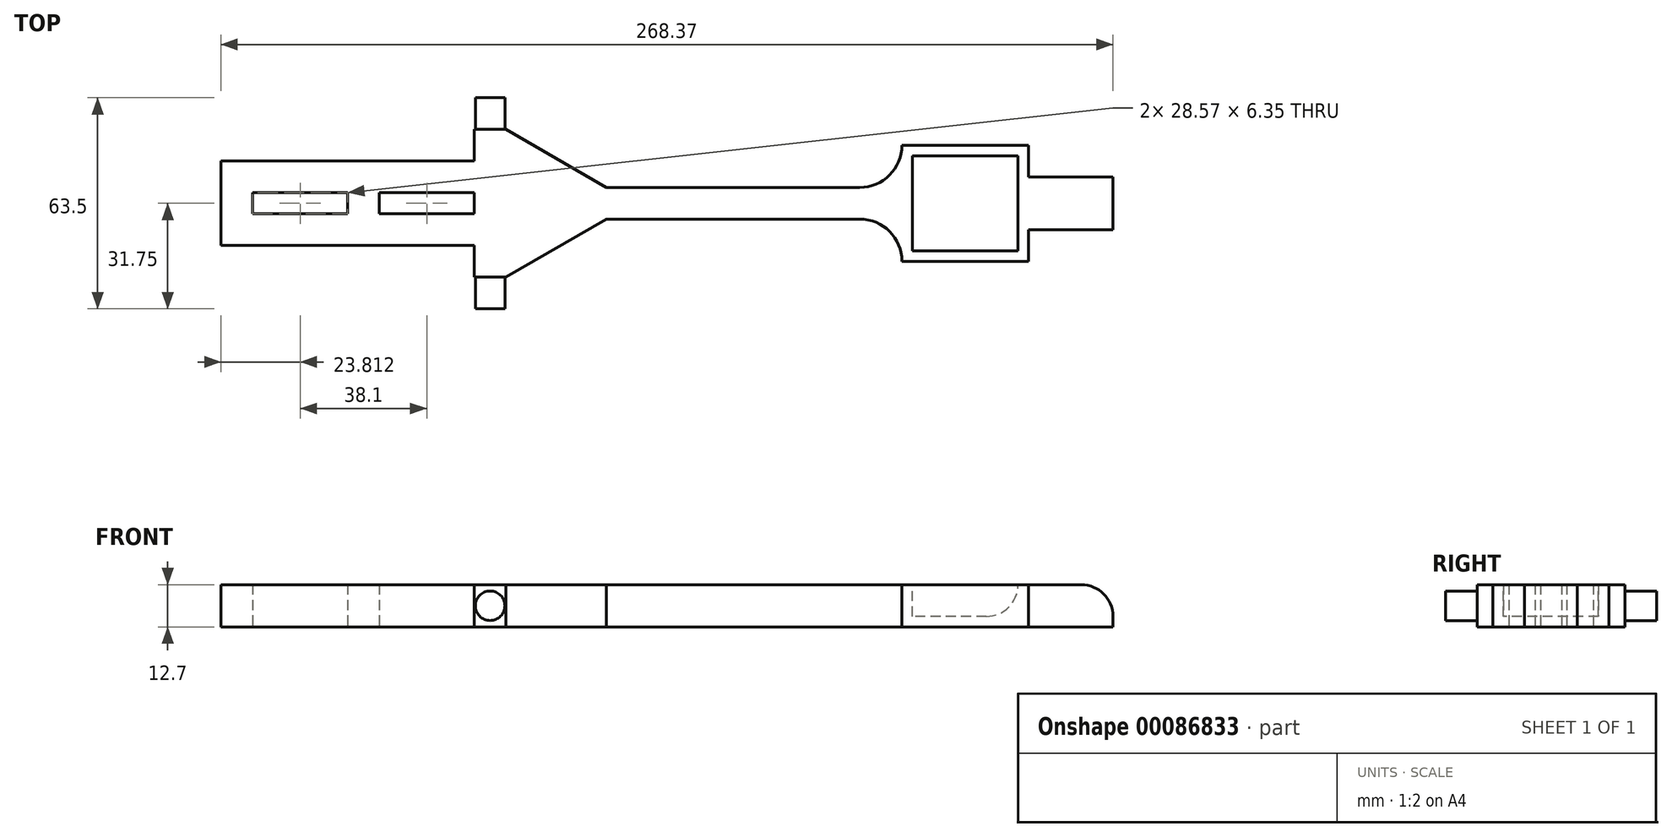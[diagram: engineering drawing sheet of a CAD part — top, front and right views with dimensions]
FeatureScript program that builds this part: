
annotation { "Feature Type Name" : "Feature", "Feature Type Description" : "" }
export const myFeature = defineFeature(function(context is Context, id is Id, definition is map)
    precondition{}
    {
        {
            var Q0;
            Q0=qCreatedBy(makeId("Top.planeOp"),FACE);
            var sketch = newSketch(context, id + "F0", { "sketchPlane" : qUnion([Q0])});
            skLineSegment(sketch, "E0.bottom", {"start": v(0, -12.7) * mm, "end": v(-76.2, -12.7) * mm});
            skLineSegment(sketch, "E0.top", {"start": v(0, 12.7) * mm, "end": v(-76.2, 12.7) * mm});
            skLineSegment(sketch, "E0.left", {"start": v(0, -3.17) * mm, "end": v(0, 3.17) * mm});
            skLineSegment(sketch, "E0.right", {"start": v(-76.2, -12.7) * mm, "end": v(-76.2, 12.7) * mm});
            skLineSegment(sketch, "E1.bottom", {"start": v(0, -3.17) * mm, "end": v(-28.58, -3.17) * mm});
            skLineSegment(sketch, "E1.top", {"start": v(0, 3.17) * mm, "end": v(-28.58, 3.17) * mm});
            skLineSegment(sketch, "E1.right", {"start": v(-28.58, -3.17) * mm, "end": v(-28.58, 3.17) * mm});
            skLineSegment(sketch, "E2.bottom", {"start": v(-66.68, 3.17) * mm, "end": v(-38.1, 3.17) * mm});
            skLineSegment(sketch, "E2.top", {"start": v(-66.68, -3.17) * mm, "end": v(-38.1, -3.17) * mm});
            skLineSegment(sketch, "E2.left", {"start": v(-66.68, 3.18) * mm, "end": v(-66.68, -3.18) * mm});
            skLineSegment(sketch, "E2.right", {"start": v(-38.1, 3.18) * mm, "end": v(-38.1, -3.18) * mm});
            skLineSegment(sketch, "E3", {"start": v(-76.2, 0) * mm, "end": v(-66.68, 0) * mm, "construction": true});
            skLineSegment(sketch, "E4", {"start": v(-52.39, 12.7) * mm, "end": v(-52.39, 3.18) * mm, "construction": true});
            skLineSegment(sketch, "E5", {"start": v(-38.1, 0) * mm, "end": v(-28.58, 0) * mm, "construction": true});
            skPoint(sketch, "E5.startSnap0", {"position": v(-38.1, 0) * mm});
            skLineSegment(sketch, "E6", {"start": v(-14.29, 3.17) * mm, "end": v(-14.29, 12.7) * mm, "construction": true});
            skLineSegment(sketch, "E7.bottom", {"start": v(0, 22.23) * mm, "end": v(9.53, 22.23) * mm});
            skLineSegment(sketch, "E7.top", {"start": v(0, -22.23) * mm, "end": v(9.53, -22.23) * mm});
            skLineSegment(sketch, "E7.left", {"start": v(0, 22.23) * mm, "end": v(0, 12.7) * mm});
            skLineSegment(sketch, "E7.right", {"start": v(9.53, 22.22) * mm, "end": v(9.53, -22.22) * mm, "construction": true});
            skLineSegment(sketch, "E8", {"start": v(-52.39, -3.18) * mm, "end": v(-52.39, -12.7) * mm, "construction": true});
            skLineSegment(sketch, "E9.trimOffspring", {"start": v(0, 3.18) * mm, "end": v(0, -3.17) * mm});
            skLineSegment(sketch, "E10.trimOffspring", {"start": v(0, -12.7) * mm, "end": v(0, -22.23) * mm});
            skPoint(sketch, "E11.endSnap0", {"position": v(9.52, 0) * mm});
            skLineSegment(sketch, "E12", {"start": v(9.52, 22.23) * mm, "end": v(39.77, 4.76) * mm});
            skLineSegment(sketch, "E13", {"start": v(39.77, -4.76) * mm, "end": v(9.52, -22.23) * mm});
            skLineSegment(sketch, "E14.bottom", {"start": v(39.77, 4.76) * mm, "end": v(115.97, 4.76) * mm});
            skLineSegment(sketch, "E14.top", {"start": v(39.77, -4.76) * mm, "end": v(115.97, -4.76) * mm});
            skLineSegment(sketch, "E14.left", {"start": v(39.77, 4.76) * mm, "end": v(39.77, -4.76) * mm, "construction": true});
            skArc(sketch, "E15", {"start": v(115.97, 4.76) * mm, "mid": v(124.95, 8.48) * mm, "end": v(128.67, 17.46) * mm});
            skArc(sketch, "E16", {"start": v(128.67, -17.46) * mm, "mid": v(124.95, -8.48) * mm, "end": v(115.97, -4.76) * mm});
            skLineSegment(sketch, "E17.bottom", {"start": v(128.67, 17.46) * mm, "end": v(166.77, 17.46) * mm});
            skLineSegment(sketch, "E17.top", {"start": v(128.67, -17.46) * mm, "end": v(166.77, -17.46) * mm});
            skLineSegment(sketch, "E17.right", {"start": v(166.77, 17.46) * mm, "end": v(166.77, 7.94) * mm});
            skLineSegment(sketch, "E18.bottom", {"start": v(166.77, 7.94) * mm, "end": v(192.17, 7.94) * mm});
            skLineSegment(sketch, "E18.top", {"start": v(166.77, -7.94) * mm, "end": v(192.17, -7.94) * mm});
            skLineSegment(sketch, "E18.right", {"start": v(192.17, 7.94) * mm, "end": v(192.17, -7.94) * mm});
            skLineSegment(sketch, "E19.trimOffspring", {"start": v(166.77, -7.94) * mm, "end": v(166.77, -17.46) * mm});
            skLineSegment(sketch, "E20", {"start": v(9.52, 0) * mm, "end": v(39.77, 0) * mm, "construction": true});
            skSolve(sketch);
        }
        {
            var Q0;
            Q0=makeQuery(id+"F0.imprint","IMPRINT",FACE,{"disambiguationData":[TD([[makeQuery(id+"F0.imprint","IMPRINT",EDGE,{"derivedFrom":sQuery(id+"F0.wireOp",EDGE,"E0.bottom")}),-1.0]])]});
            extrude(context, id + "F1", {"entities" : qUnion([Q0]), "depth" : 12.7 * mm});
        }
        {
            var Q0;
            Q0=makeQuery(id+"F1.opExtrude","SWEPT_FACE",FACE,{"disambiguationData":[OSD([sQuery(id+"F0.wireOp",EDGE,"E7.top")])]});
            var sketch = newSketch(context, id + "F2", { "sketchPlane" : qUnion([Q0])});
            skCircle(sketch, "E21", {"center": v(4.76, 6.35) * mm, "radius": 4.45 * mm});
            skPoint(sketch, "E21.centerSnap0", {"position": v(4.76, 12.7) * mm});
            skLineSegment(sketch, "E22", {"start": v(0, 12.7) * mm, "end": v(9.52, 0) * mm, "construction": true});
            skSolve(sketch);
        }
        {
            var Q0;
            Q0=makeQuery(id+"F2.imprint","IMPRINT",FACE,{"disambiguationData":[TD([[makeQuery(id+"F2.imprint","IMPRINT",EDGE,{"derivedFrom":sQuery(id+"F2.wireOp",EDGE,"E21")}),1.0]])]});
            extrude(context, id + "F3", {"entities" : qUnion([Q0]), "operationType" : NewBodyOperationType.ADD, "depth" : 9.52 * mm});
        }
        {
            var Q0;
            Q0=makeQuery(id+"F1.opExtrude","SWEPT_FACE",FACE,{"disambiguationData":[OSD([sQuery(id+"F0.wireOp",EDGE,"E7.bottom")])]});
            var sketch = newSketch(context, id + "F4", { "sketchPlane" : qUnion([Q0])});
            skCircle(sketch, "E23.0", {"center": v(-4.76, 6.35) * mm, "radius": 4.45 * mm});
            skSolve(sketch);
        }
        {
            var Q0;
            Q0 = qSketchRegion(id + "F4", true);
            extrude(context, id + "F5", {"entities" : qUnion([Q0]), "operationType" : NewBodyOperationType.ADD, "depth" : 9.52 * mm});
        }
        {
            var Q0;
            Q0=makeQuery(id+"F1.opExtrude","CAP_FACE",FACE,{"disambiguationData":[OSD([sQuery(id+"F0.wireOp",EDGE,"E0.bottom"),sQuery(id+"F0.wireOp",EDGE,"E0.top"),sQuery(id+"F0.wireOp",EDGE,"E0.right"),sQuery(id+"F0.wireOp",EDGE,"E1.bottom"),sQuery(id+"F0.wireOp",EDGE,"E1.top"),sQuery(id+"F0.wireOp",EDGE,"E1.right"),sQuery(id+"F0.wireOp",EDGE,"E2.bottom"),sQuery(id+"F0.wireOp",EDGE,"E2.top"),sQuery(id+"F0.wireOp",EDGE,"E2.left"),sQuery(id+"F0.wireOp",EDGE,"E2.right"),sQuery(id+"F0.wireOp",EDGE,"E7.bottom"),sQuery(id+"F0.wireOp",EDGE,"E7.top"),sQuery(id+"F0.wireOp",EDGE,"E7.left"),sQuery(id+"F0.wireOp",EDGE,"E9.trimOffspring"),sQuery(id+"F0.wireOp",EDGE,"E10.trimOffspring"),sQuery(id+"F0.wireOp",EDGE,"E12"),sQuery(id+"F0.wireOp",EDGE,"E13"),sQuery(id+"F0.wireOp",EDGE,"E14.bottom"),sQuery(id+"F0.wireOp",EDGE,"E14.top"),sQuery(id+"F0.wireOp",EDGE,"E15"),sQuery(id+"F0.wireOp",EDGE,"E16"),sQuery(id+"F0.wireOp",EDGE,"E17.bottom"),sQuery(id+"F0.wireOp",EDGE,"E17.top"),sQuery(id+"F0.wireOp",EDGE,"E17.right"),sQuery(id+"F0.wireOp",EDGE,"E18.bottom"),sQuery(id+"F0.wireOp",EDGE,"E18.top"),sQuery(id+"F0.wireOp",EDGE,"E18.right"),sQuery(id+"F0.wireOp",EDGE,"E19.trimOffspring")])],"isStart":false});
            var sketch = newSketch(context, id + "F6", { "sketchPlane" : qUnion([Q0])});
            skLineSegment(sketch, "E24.bottom", {"start": v(163.6, 14.29) * mm, "end": v(131.85, 14.29) * mm});
            skLineSegment(sketch, "E24.top", {"start": v(163.6, -14.29) * mm, "end": v(131.85, -14.29) * mm});
            skLineSegment(sketch, "E24.left", {"start": v(163.6, 14.29) * mm, "end": v(163.6, -14.29) * mm});
            skLineSegment(sketch, "E24.right", {"start": v(131.85, 14.29) * mm, "end": v(131.85, -14.29) * mm});
            skPoint(sketch, "E24.middle", {"position": v(147.72, 0) * mm});
            skLineSegment(sketch, "E25", {"start": v(147.72, 17.46) * mm, "end": v(147.72, 14.29) * mm, "construction": true});
            skLineSegment(sketch, "E26", {"start": v(166.77, -7.94) * mm, "end": v(163.6, -7.94) * mm, "construction": true});
            skLineSegment(sketch, "E27", {"start": v(128.67, 17.46) * mm, "end": v(166.77, -17.46) * mm, "construction": true});
            skSolve(sketch);
        }
        {
            var Q0;
            Q0=makeQuery(id+"F6.imprint","IMPRINT",FACE,{"disambiguationData":[TD([[makeQuery(id+"F6.imprint","IMPRINT",EDGE,{"derivedFrom":sQuery(id+"F6.wireOp",EDGE,"E24.bottom")}),1.0]])]});
            extrude(context, id + "F7", {"entities" : qUnion([Q0]), "operationType" : NewBodyOperationType.REMOVE, "oppositeDirection" : true, "depth" : 9.52 * mm});
        }
        {
            var Q0;
            Q0=makeQuery(id+"F7.boolean.opBoolean","COPY",EDGE,{"derivedFrom":makeQuery(id+"F7.opExtrude","CAP_EDGE",EDGE,{"disambiguationData":[OSD([sQuery(id+"F6.wireOp",EDGE,"E24.left")])],"isStart":false})});
            var Q1;
            Q1=makeQuery(id+"F1.opExtrude","CAP_EDGE",EDGE,{"disambiguationData":[OSD([sQuery(id+"F0.wireOp",EDGE,"E18.right")])],"isStart":false});
            fillet(context, id + "F8", {"entities" : qUnion([Q0, Q1]), "radius" : 9.52 * mm, "tangentPropagation" : true, "allowEdgeOverflow" : false});
        }
    });
